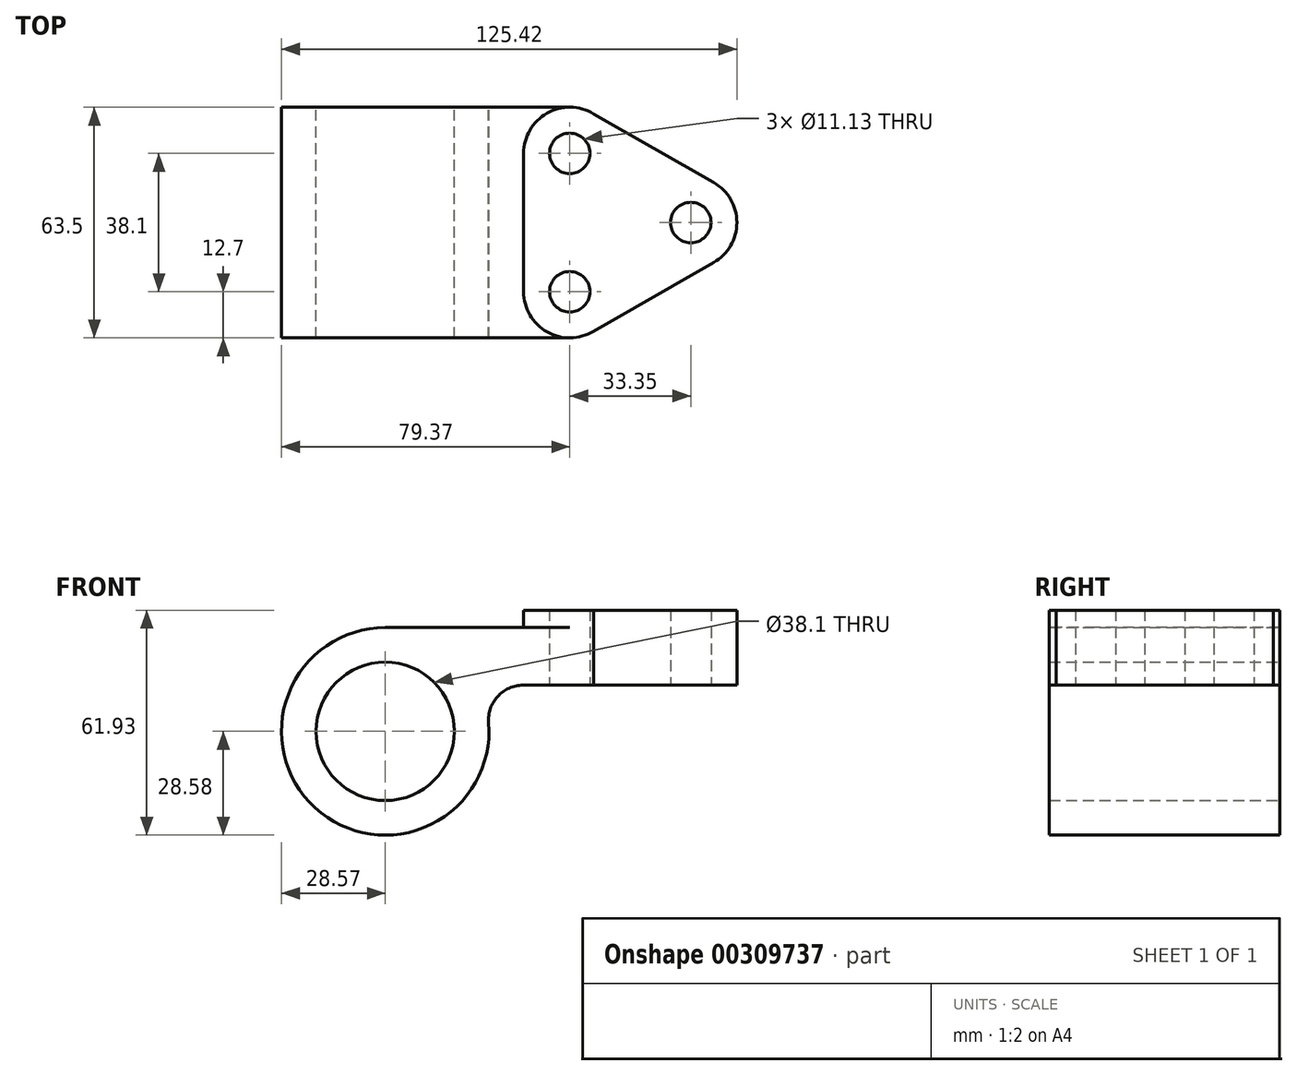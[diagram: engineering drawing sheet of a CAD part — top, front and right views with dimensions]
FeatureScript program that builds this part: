
annotation { "Feature Type Name" : "Feature", "Feature Type Description" : "" }
export const myFeature = defineFeature(function(context is Context, id is Id, definition is map)
    precondition{}
    {
        {
            var Q0;
            Q0=qCreatedBy(makeId("Front.planeOp"),FACE);
            var sketch = newSketch(context, id + "F0", { "sketchPlane" : qUnion([Q0])});
            skCircle(sketch, "E0", {"center": v(0, 0) * mm, "radius": 19.05 * mm});
            skLineSegment(sketch, "E1", {"start": v(50.8, 12.7) * mm, "end": v(50.8, 28.58) * mm});
            skArc(sketch, "E2", {"start": v(0, 28.58) * mm, "mid": v(-19.35, -21.03) * mm, "end": v(28.48, 2.38) * mm});
            skLineSegment(sketch, "E3", {"start": v(50.8, 12.7) * mm, "end": v(37.97, 12.7) * mm});
            skArc(sketch, "E4", {"start": v(37.97, 12.7) * mm, "mid": v(30.96, 9.62) * mm, "end": v(28.48, 2.38) * mm});
            skLineSegment(sketch, "E5", {"start": v(0, 28.58) * mm, "end": v(50.8, 28.58) * mm});
            skSolve(sketch);
        }
        {
            var Q0;
            Q0 = qSketchRegion(id + "F0", true);
            extrude(context, id + "F1", {"entities" : qUnion([Q0]), "depth" : 63.5 * mm});
        }
        {
            var Q0;
            Q0=makeQuery(id+"F1.opExtrude","SWEPT_FACE",FACE,{"disambiguationData":[OSD([sQuery(id+"F0.wireOp",EDGE,"E5")])]});
            var sketch = newSketch(context, id + "F2", { "sketchPlane" : qUnion([Q0])});
            skCircle(sketch, "E6", {"center": v(50.8, -12.7) * mm, "radius": 5.56 * mm});
            skCircle(sketch, "E7", {"center": v(50.8, -50.8) * mm, "radius": 5.56 * mm});
            skLineSegment(sketch, "E8", {"start": v(0, -31.75) * mm, "end": v(9.72, -31.75) * mm, "construction": true});
            skLineSegment(sketch, "E9", {"start": v(50.8, -12.7) * mm, "end": v(43.42, -12.7) * mm, "construction": true});
            skLineSegment(sketch, "E10", {"start": v(50.8, -50.8) * mm, "end": v(36.16, -50.8) * mm, "construction": true});
            skCircle(sketch, "E11", {"center": v(84.15, -31.75) * mm, "radius": 5.56 * mm});
            skLineSegment(sketch, "E12", {"start": v(38.1, -12.7) * mm, "end": v(38.1, -50.8) * mm});
            skPoint(sketch, "E12.startSnap0", {"position": v(47.1, -12.7) * mm});
            skArc(sketch, "E13", {"start": v(38.1, -12.7) * mm, "mid": v(44.56, -1.64) * mm, "end": v(57.36, -1.83) * mm});
            skArc(sketch, "E14", {"start": v(38.1, -50.8) * mm, "mid": v(44.56, -61.86) * mm, "end": v(57.36, -61.67) * mm});
            skLineSegment(sketch, "E15", {"start": v(57.36, -1.83) * mm, "end": v(90.45, -20.72) * mm});
            skArc(sketch, "E16", {"start": v(90.45, -20.72) * mm, "mid": v(96.85, -31.75) * mm, "end": v(90.45, -42.78) * mm});
            skLineSegment(sketch, "E17", {"start": v(57.36, -61.67) * mm, "end": v(90.45, -42.78) * mm});
            skSolve(sketch);
        }
        {
            var Q0;
            Q0 = qSketchRegion(id + "F2", true);
            extrude(context, id + "F3", {"entities" : qUnion([Q0]), "operationType" : NewBodyOperationType.ADD, "depth" : 4.78 * mm});
        }
        {
            var Q0;
            Q0=makeQuery(id+"F3.opExtrude","CAP_FACE",FACE,{"disambiguationData":[OSD([sQuery(id+"F2.wireOp",EDGE,"E6"),sQuery(id+"F2.wireOp",EDGE,"E7"),sQuery(id+"F2.wireOp",EDGE,"E11"),sQuery(id+"F2.wireOp",EDGE,"E12"),sQuery(id+"F2.wireOp",EDGE,"E13"),sQuery(id+"F2.wireOp",EDGE,"E14"),sQuery(id+"F2.wireOp",EDGE,"E15"),sQuery(id+"F2.wireOp",EDGE,"E16"),sQuery(id+"F2.wireOp",EDGE,"E17")])],"isStart":true});
            var sketch = newSketch(context, id + "F4", { "sketchPlane" : qUnion([Q0])});
            skArc(sketch, "E18.0.0", {"start": v(57.36, 61.67) * mm, "mid": v(54.2, 63.03) * mm, "end": v(50.8, 63.5) * mm});
            skLineSegment(sketch, "E18.0.1", {"start": v(50.8, 63.5) * mm, "end": v(50.8, 56.36) * mm});
            skArc(sketch, "E18.0.2", {"start": v(50.8, 56.36) * mm, "mid": v(56.36, 50.8) * mm, "end": v(50.8, 45.24) * mm});
            skLineSegment(sketch, "E18.0.3", {"start": v(50.8, 45.24) * mm, "end": v(50.8, 18.26) * mm});
            skArc(sketch, "E18.0.4", {"start": v(50.8, 18.26) * mm, "mid": v(56.36, 12.7) * mm, "end": v(50.8, 7.14) * mm});
            skLineSegment(sketch, "E18.0.5", {"start": v(50.8, 7.14) * mm, "end": v(50.8, 0) * mm});
            skArc(sketch, "E18.0.6", {"start": v(50.8, 0) * mm, "mid": v(54.2, 0.47) * mm, "end": v(57.36, 1.83) * mm});
            skLineSegment(sketch, "E18.0.7", {"start": v(57.36, 1.83) * mm, "end": v(90.45, 20.72) * mm});
            skArc(sketch, "E18.0.8", {"start": v(90.45, 20.72) * mm, "mid": v(96.85, 31.75) * mm, "end": v(90.45, 42.78) * mm});
            skLineSegment(sketch, "E18.0.9", {"start": v(90.45, 42.78) * mm, "end": v(57.36, 61.67) * mm});
            skSolve(sketch);
        }
        {
            var Q0;
            Q0=makeQuery(id+"F4.imprint","IMPRINT",FACE,{"disambiguationData":[TD([[makeQuery(id+"F4.imprint","IMPRINT",EDGE,{"derivedFrom":sQuery(id+"F4.wireOp",EDGE,"E18.0.0")}),-1.0]])]});
            var sketch = newSketch(context, id + "F5", { "sketchPlane" : qUnion([Q0])});
            skArc(sketch, "E19.0.0", {"start": v(57.36, 61.67) * mm, "mid": v(54.2, 63.03) * mm, "end": v(50.8, 63.5) * mm});
            skLineSegment(sketch, "E19.0.1", {"start": v(50.8, 63.5) * mm, "end": v(50.8, 56.36) * mm});
            skArc(sketch, "E19.0.2", {"start": v(50.8, 56.36) * mm, "mid": v(56.36, 50.8) * mm, "end": v(50.8, 45.24) * mm});
            skLineSegment(sketch, "E19.0.3", {"start": v(50.8, 45.24) * mm, "end": v(50.8, 18.26) * mm});
            skArc(sketch, "E19.0.4", {"start": v(50.8, 18.26) * mm, "mid": v(56.36, 12.7) * mm, "end": v(50.8, 7.14) * mm});
            skLineSegment(sketch, "E19.0.5", {"start": v(50.8, 7.14) * mm, "end": v(50.8, 0) * mm});
            skArc(sketch, "E19.0.6", {"start": v(50.8, 0) * mm, "mid": v(54.2, 0.47) * mm, "end": v(57.36, 1.83) * mm});
            skLineSegment(sketch, "E19.0.7", {"start": v(57.36, 1.83) * mm, "end": v(90.45, 20.72) * mm});
            skArc(sketch, "E19.0.8", {"start": v(90.45, 20.72) * mm, "mid": v(96.85, 31.75) * mm, "end": v(90.45, 42.78) * mm});
            skLineSegment(sketch, "E19.0.9", {"start": v(90.45, 42.78) * mm, "end": v(57.36, 61.67) * mm});
            skSolve(sketch);
        }
        {
            var Q0;
            Q0 = qSketchRegion(id + "F5", true);
            var Q1;
            Q1 = qSketchRegion(id + "F4", true);
            extrude(context, id + "F6", {"entities" : qUnion([Q0, Q1]), "operationType" : NewBodyOperationType.ADD, "depth" : 15.88 * mm});
        }
        {
            var Q0;
            {var subQ0=sQuery(id+"F2.wireOp",EDGE,"E7");Q0=makeQuery(id+"F3.boolean.opBoolean","SPLIT",FACE,{"disambiguationData":[TD([makeQuery(id+"F3.opExtrude","SWEPT_FACE",FACE,{"disambiguationData":[OSD([subQ0])]})])],"derivedFrom":makeQuery(id+"F1.opExtrude","SWEPT_FACE",FACE,{"disambiguationData":[OSD([sQuery(id+"F0.wireOp",EDGE,"E5")])]})});}
            var sketch = newSketch(context, id + "F7", { "sketchPlane" : qUnion([Q0])});
            skCircle(sketch, "E20", {"center": v(50.8, -50.8) * mm, "radius": 5.56 * mm});
            skCircle(sketch, "E21", {"center": v(50.8, -12.7) * mm, "radius": 5.56 * mm});
            skCircle(sketch, "E22", {"center": v(84.15, -31.75) * mm, "radius": 5.56 * mm});
            skSolve(sketch);
        }
        {
            var Q0;
            Q0 = qSketchRegion(id + "F7", true);
            extrude(context, id + "F8", {"entities" : qUnion([Q0]), "operationType" : NewBodyOperationType.REMOVE, "endBound" : BoundingType.THROUGH_ALL, "oppositeDirection" : true, "depth" : 25.4 * mm});
        }
    });
